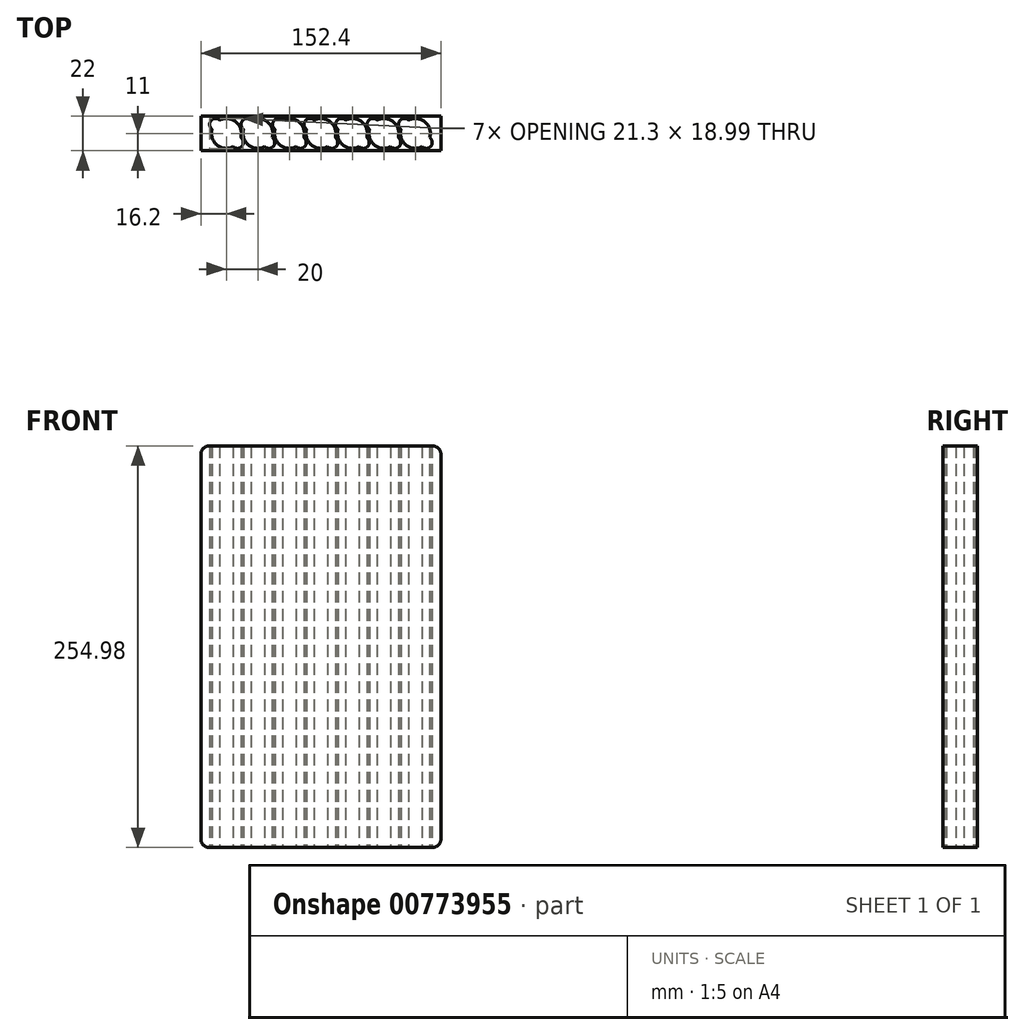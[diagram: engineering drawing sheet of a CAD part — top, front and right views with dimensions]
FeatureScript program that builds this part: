
annotation { "Feature Type Name" : "Feature", "Feature Type Description" : "" }
export const myFeature = defineFeature(function(context is Context, id is Id, definition is map)
    precondition{}
    {
        {
            var Q0;
            Q0=qCreatedBy(makeId("Top.planeOp"),FACE);
            var sketch = newSketch(context, id + "F0", { "sketchPlane" : qUnion([Q0])});
            skLineSegment(sketch, "E0.bottom", {"start": v(76.2, 11) * mm, "end": v(-76.2, 11) * mm});
            skLineSegment(sketch, "E0.top", {"start": v(76.2, -11) * mm, "end": v(-76.2, -11) * mm});
            skLineSegment(sketch, "E0.left", {"start": v(76.2, 11) * mm, "end": v(76.2, -11) * mm});
            skLineSegment(sketch, "E0.right", {"start": v(-76.2, 11) * mm, "end": v(-76.2, -11) * mm});
            skPoint(sketch, "E0.middle", {"position": v(0, 0) * mm});
            skArc(sketch, "E1", {"start": v(-9.13, 2.62) * mm, "mid": v(-6.06, -7.32) * mm, "end": v(4.28, -8.48) * mm});
            skPoint(sketch, "E2.start.orphan", {"position": v(0, -9.5) * mm});
            skArc(sketch, "E3", {"start": v(4.28, -8.48) * mm, "mid": v(9.8, -8.12) * mm, "end": v(9.13, -2.62) * mm});
            skArc(sketch, "E4.1.0", {"start": v(-4.28, 8.48) * mm, "mid": v(-9.8, 8.12) * mm, "end": v(-9.13, 2.62) * mm});
            skArc(sketch, "E5.trimOffspring", {"start": v(9.13, -2.62) * mm, "mid": v(6.06, 7.32) * mm, "end": v(-4.28, 8.48) * mm});
            skArc(sketch, "E6.1.0.0", {"start": v(29.13, -2.62) * mm, "mid": v(26.06, 7.32) * mm, "end": v(15.72, 8.48) * mm});
            skArc(sketch, "E6.1.0.1", {"start": v(10.87, 2.62) * mm, "mid": v(13.94, -7.32) * mm, "end": v(24.28, -8.48) * mm});
            skArc(sketch, "E6.1.0.2", {"start": v(15.72, 8.48) * mm, "mid": v(10.2, 8.12) * mm, "end": v(10.87, 2.62) * mm});
            skArc(sketch, "E6.1.0.3", {"start": v(24.28, -8.48) * mm, "mid": v(29.8, -8.12) * mm, "end": v(29.13, -2.62) * mm});
            skArc(sketch, "E6.2.0.0", {"start": v(49.13, -2.62) * mm, "mid": v(46.06, 7.32) * mm, "end": v(35.72, 8.48) * mm});
            skArc(sketch, "E6.2.0.1", {"start": v(30.87, 2.62) * mm, "mid": v(33.94, -7.32) * mm, "end": v(44.28, -8.48) * mm});
            skArc(sketch, "E6.2.0.2", {"start": v(35.72, 8.48) * mm, "mid": v(30.2, 8.12) * mm, "end": v(30.87, 2.62) * mm});
            skArc(sketch, "E6.2.0.3", {"start": v(44.28, -8.48) * mm, "mid": v(49.8, -8.12) * mm, "end": v(49.13, -2.62) * mm});
            skArc(sketch, "E6.3.0.0", {"start": v(69.13, -2.62) * mm, "mid": v(66.06, 7.32) * mm, "end": v(55.72, 8.48) * mm});
            skArc(sketch, "E6.3.0.1", {"start": v(50.87, 2.62) * mm, "mid": v(53.94, -7.32) * mm, "end": v(64.28, -8.48) * mm});
            skArc(sketch, "E6.3.0.2", {"start": v(55.72, 8.48) * mm, "mid": v(50.2, 8.12) * mm, "end": v(50.87, 2.62) * mm});
            skArc(sketch, "E6.3.0.3", {"start": v(64.28, -8.48) * mm, "mid": v(69.8, -8.12) * mm, "end": v(69.13, -2.62) * mm});
            skLineSegment(sketch, "E6.direction1", {"start": v(-9.13, 2.62) * mm, "end": v(10.87, 2.62) * mm, "construction": true});
            skArc(sketch, "E7.1.0.0", {"start": v(-10.87, -2.62) * mm, "mid": v(-13.94, 7.32) * mm, "end": v(-24.28, 8.48) * mm});
            skArc(sketch, "E7.1.0.1", {"start": v(-29.13, 2.62) * mm, "mid": v(-26.06, -7.32) * mm, "end": v(-15.72, -8.48) * mm});
            skArc(sketch, "E7.1.0.2", {"start": v(-24.28, 8.48) * mm, "mid": v(-29.8, 8.12) * mm, "end": v(-29.13, 2.62) * mm});
            skArc(sketch, "E7.1.0.3", {"start": v(-15.72, -8.48) * mm, "mid": v(-10.2, -8.12) * mm, "end": v(-10.87, -2.62) * mm});
            skArc(sketch, "E7.2.0.0", {"start": v(-30.87, -2.62) * mm, "mid": v(-33.94, 7.32) * mm, "end": v(-44.28, 8.48) * mm});
            skArc(sketch, "E7.2.0.1", {"start": v(-49.13, 2.62) * mm, "mid": v(-46.06, -7.32) * mm, "end": v(-35.72, -8.48) * mm});
            skArc(sketch, "E7.2.0.2", {"start": v(-44.28, 8.48) * mm, "mid": v(-49.8, 8.12) * mm, "end": v(-49.13, 2.62) * mm});
            skArc(sketch, "E7.2.0.3", {"start": v(-35.72, -8.48) * mm, "mid": v(-30.2, -8.12) * mm, "end": v(-30.87, -2.62) * mm});
            skArc(sketch, "E7.3.0.0", {"start": v(-50.87, -2.62) * mm, "mid": v(-53.94, 7.32) * mm, "end": v(-64.28, 8.48) * mm});
            skArc(sketch, "E7.3.0.1", {"start": v(-69.13, 2.62) * mm, "mid": v(-66.06, -7.32) * mm, "end": v(-55.72, -8.48) * mm});
            skArc(sketch, "E7.3.0.2", {"start": v(-64.28, 8.48) * mm, "mid": v(-69.8, 8.12) * mm, "end": v(-69.13, 2.62) * mm});
            skArc(sketch, "E7.3.0.3", {"start": v(-55.72, -8.48) * mm, "mid": v(-50.2, -8.12) * mm, "end": v(-50.87, -2.62) * mm});
            skLineSegment(sketch, "E7.direction1", {"start": v(-9.13, 2.62) * mm, "end": v(-29.13, 2.62) * mm, "construction": true});
            skSolve(sketch);
        }
        {
            var Q0;
            Q0 = qSketchRegion(id + "F0", true);
            extrude(context, id + "F1", {"entities" : qUnion([Q0]), "depth" : 254.98 * mm, "offsetDistance" : 25.4 * mm});
        }
        {
            var Q0;
            Q0=makeQuery(id+"F1.opExtrude","CAP_EDGE",EDGE,{"disambiguationData":[OSD([sQuery(id+"F0.wireOp",EDGE,"E0.left")])],"isStart":false});
            var Q1;
            Q1=makeQuery(id+"F1.opExtrude","CAP_EDGE",EDGE,{"disambiguationData":[OSD([sQuery(id+"F0.wireOp",EDGE,"E0.right")])],"isStart":false});
            var Q2;
            Q2=makeQuery(id+"F1.opExtrude","CAP_EDGE",EDGE,{"disambiguationData":[OSD([sQuery(id+"F0.wireOp",EDGE,"E0.left")])],"isStart":true});
            var Q3;
            Q3=makeQuery(id+"F1.opExtrude","CAP_EDGE",EDGE,{"disambiguationData":[OSD([sQuery(id+"F0.wireOp",EDGE,"E0.right")])],"isStart":true});
            fillet(context, id + "F2", {"entities" : qUnion([Q0, Q1, Q2, Q3]), "radius" : 5.08 * mm, "tangentPropagation" : true, "allowEdgeOverflow" : false});
        }
    });
